# Revit family: Кровать больничная
name_source: partatom
category: Специальное оборудование
revit_build: Autodesk Revit 2017 (Build: 20170419_0315(x64)
units: mm (PartAtom-declared; Revit-internal decimal feet)

## family parameters
Всегда вертикально = Да
Заголовок OmniClass = Patient Beds
На основе рабочей плоскости = Нет
Номер OmniClass = 23.40.70.11.14.11.17.17
Общий = Нет
При загрузке вырезать с полостями = Нет
Размер круглого соединителя = Использовать диаметр
Тип детали = Нормальный
Точка расчета площади = Нет

## types (1)
- Тип
    Bed Finish = Textile-Hill Rom-Matress
    Frame Finish = Plastic-Hill-Rom-Light Beige
    Общ_Высота = 1003 мм
    Общ_Глубина = 1016 мм
    Общ_Единицы измерения = шт.
    Общ_Задание = ЭМ
    Общ_Масса = 150
    Общ_Мощность номинальная = 350 Вт
    Общ_Наименование = Кровать больничная
    Общ_Напряжение = 220 В
    Общ_Поставщик = Linet
    Общ_Тип, марка = Eleganza
    Общ_Ширина = 2400 мм

## geometry (parser evidence)
native form markers: Blend x20, Sweep x3
no freeform markers — native parametric forms only
